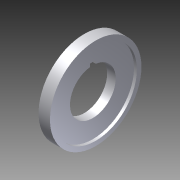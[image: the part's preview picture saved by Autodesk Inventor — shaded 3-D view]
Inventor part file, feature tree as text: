
AUTODESK INVENTOR PART (.ipt)
format: ipt  version: 2012 (Build 160160000, 160)  size: 611,328 bytes
history: native  units: in
note: dims shown in document units (in); Inventor stores cm internally (conversion verified against a paired STEP export)
features: extrude x2, sketch x1, imported_body x1
ambient origin geometry x8: Origin, YZ Plane, XZ Plane, XY Plane, X Axis, Y Axis, Z Axis, Center Point
feature tree (4):
  sketch  "Sketch1"  dims[d0=0.375in d3=0.3in d4=0.0in d5=1.0in d6=0.125in d7=0.125in d8=0.0625in d9=0.5625in d10=2.0in d11=1.0in d12=0.0in]
  extrude  "Extrusion2"  Depth=0.3in TaperAngle=0.0deg
  extrude  "Extrusion3"  Depth=1.0in
  imported_body  "Base1"
